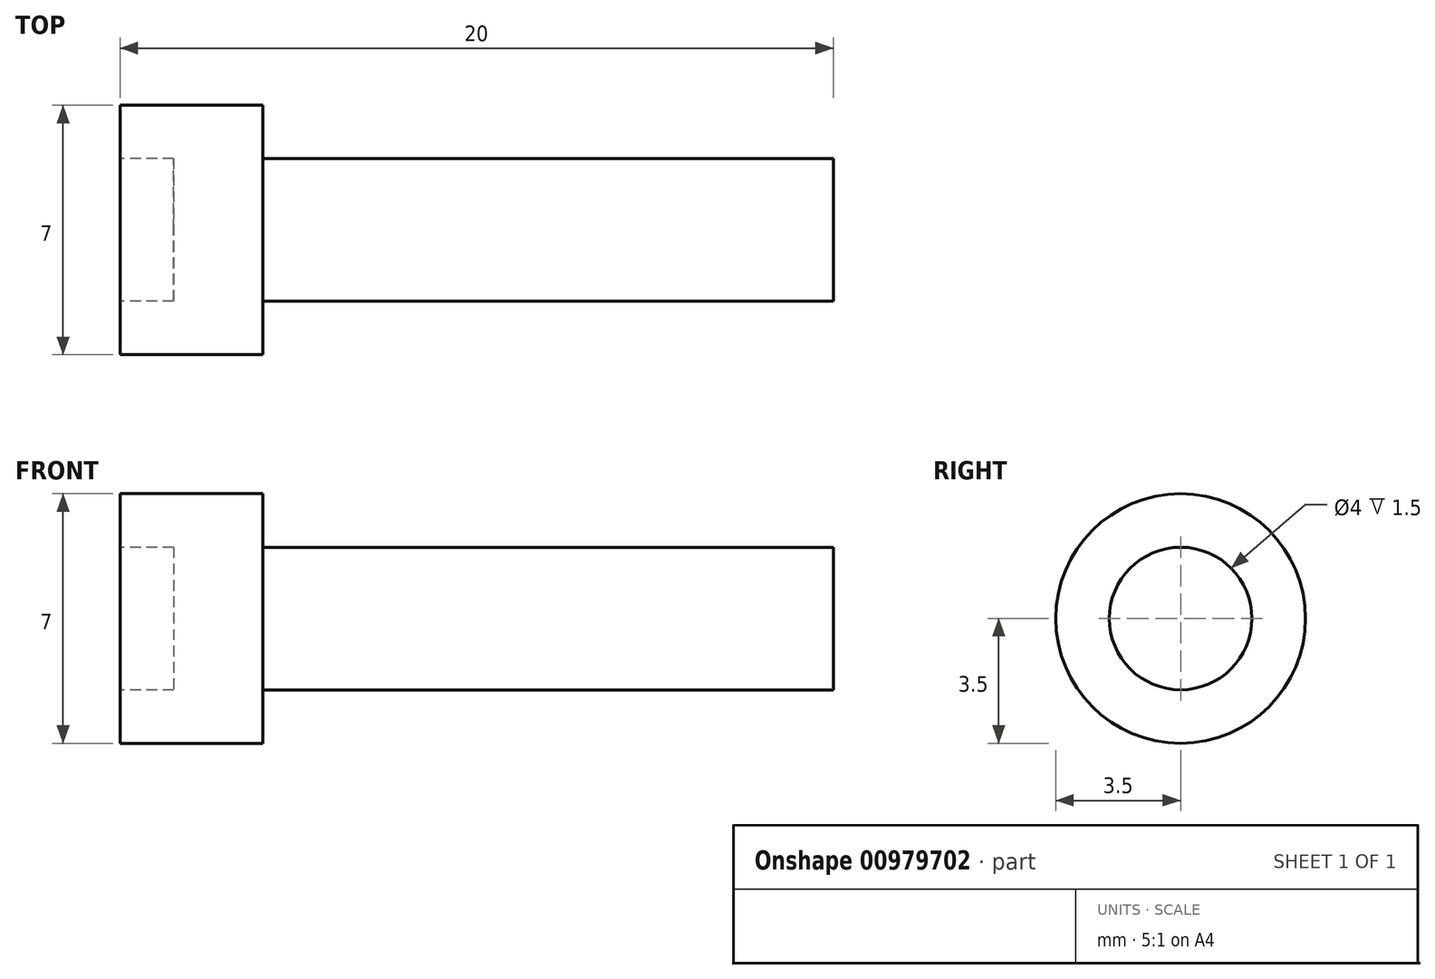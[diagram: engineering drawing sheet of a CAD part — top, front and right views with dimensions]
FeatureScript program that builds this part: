
annotation { "Feature Type Name" : "Feature", "Feature Type Description" : "" }
export const myFeature = defineFeature(function(context is Context, id is Id, definition is map)
    precondition{}
    {
        {
            var Q0;
            Q0=qCreatedBy(makeId("Front.planeOp"),FACE);
            var sketch = newSketch(context, id + "F0", { "sketchPlane" : qUnion([Q0])});
            skLineSegment(sketch, "E0.bottom", {"start": v(0, 0) * mm, "end": v(-2.5, 0) * mm});
            skLineSegment(sketch, "E0.top", {"start": v(0, 3.5) * mm, "end": v(-4, 3.5) * mm});
            skLineSegment(sketch, "E0.left", {"start": v(0, 2) * mm, "end": v(0, 3.5) * mm});
            skLineSegment(sketch, "E0.right", {"start": v(-4, 2) * mm, "end": v(-4, 3.5) * mm});
            skLineSegment(sketch, "E1.bottom", {"start": v(0, 0) * mm, "end": v(16, 0) * mm});
            skLineSegment(sketch, "E1.top", {"start": v(0, 2) * mm, "end": v(16, 2) * mm});
            skLineSegment(sketch, "E1.right", {"start": v(16, 0) * mm, "end": v(16, 2) * mm});
            skLineSegment(sketch, "E2.top", {"start": v(-4, 2) * mm, "end": v(-2.5, 2) * mm});
            skLineSegment(sketch, "E2.right", {"start": v(-2.5, 0) * mm, "end": v(-2.5, 2) * mm});
            skSolve(sketch);
        }
        {
            var Q0;
            Q0 = qSketchRegion(id + "F0", true);
            var Q1;
            Q1=sQuery(id+"F0.wireOp",EDGE,"E1.bottom");
            revolve(context, id + "F1", {"surfaceOperationType" : NewSurfaceOperationType.NEW, "entities" : qUnion([Q0]), "axis" : qUnion([Q1]), "revolveType" : RevolveType.FULL});
        }
    });
